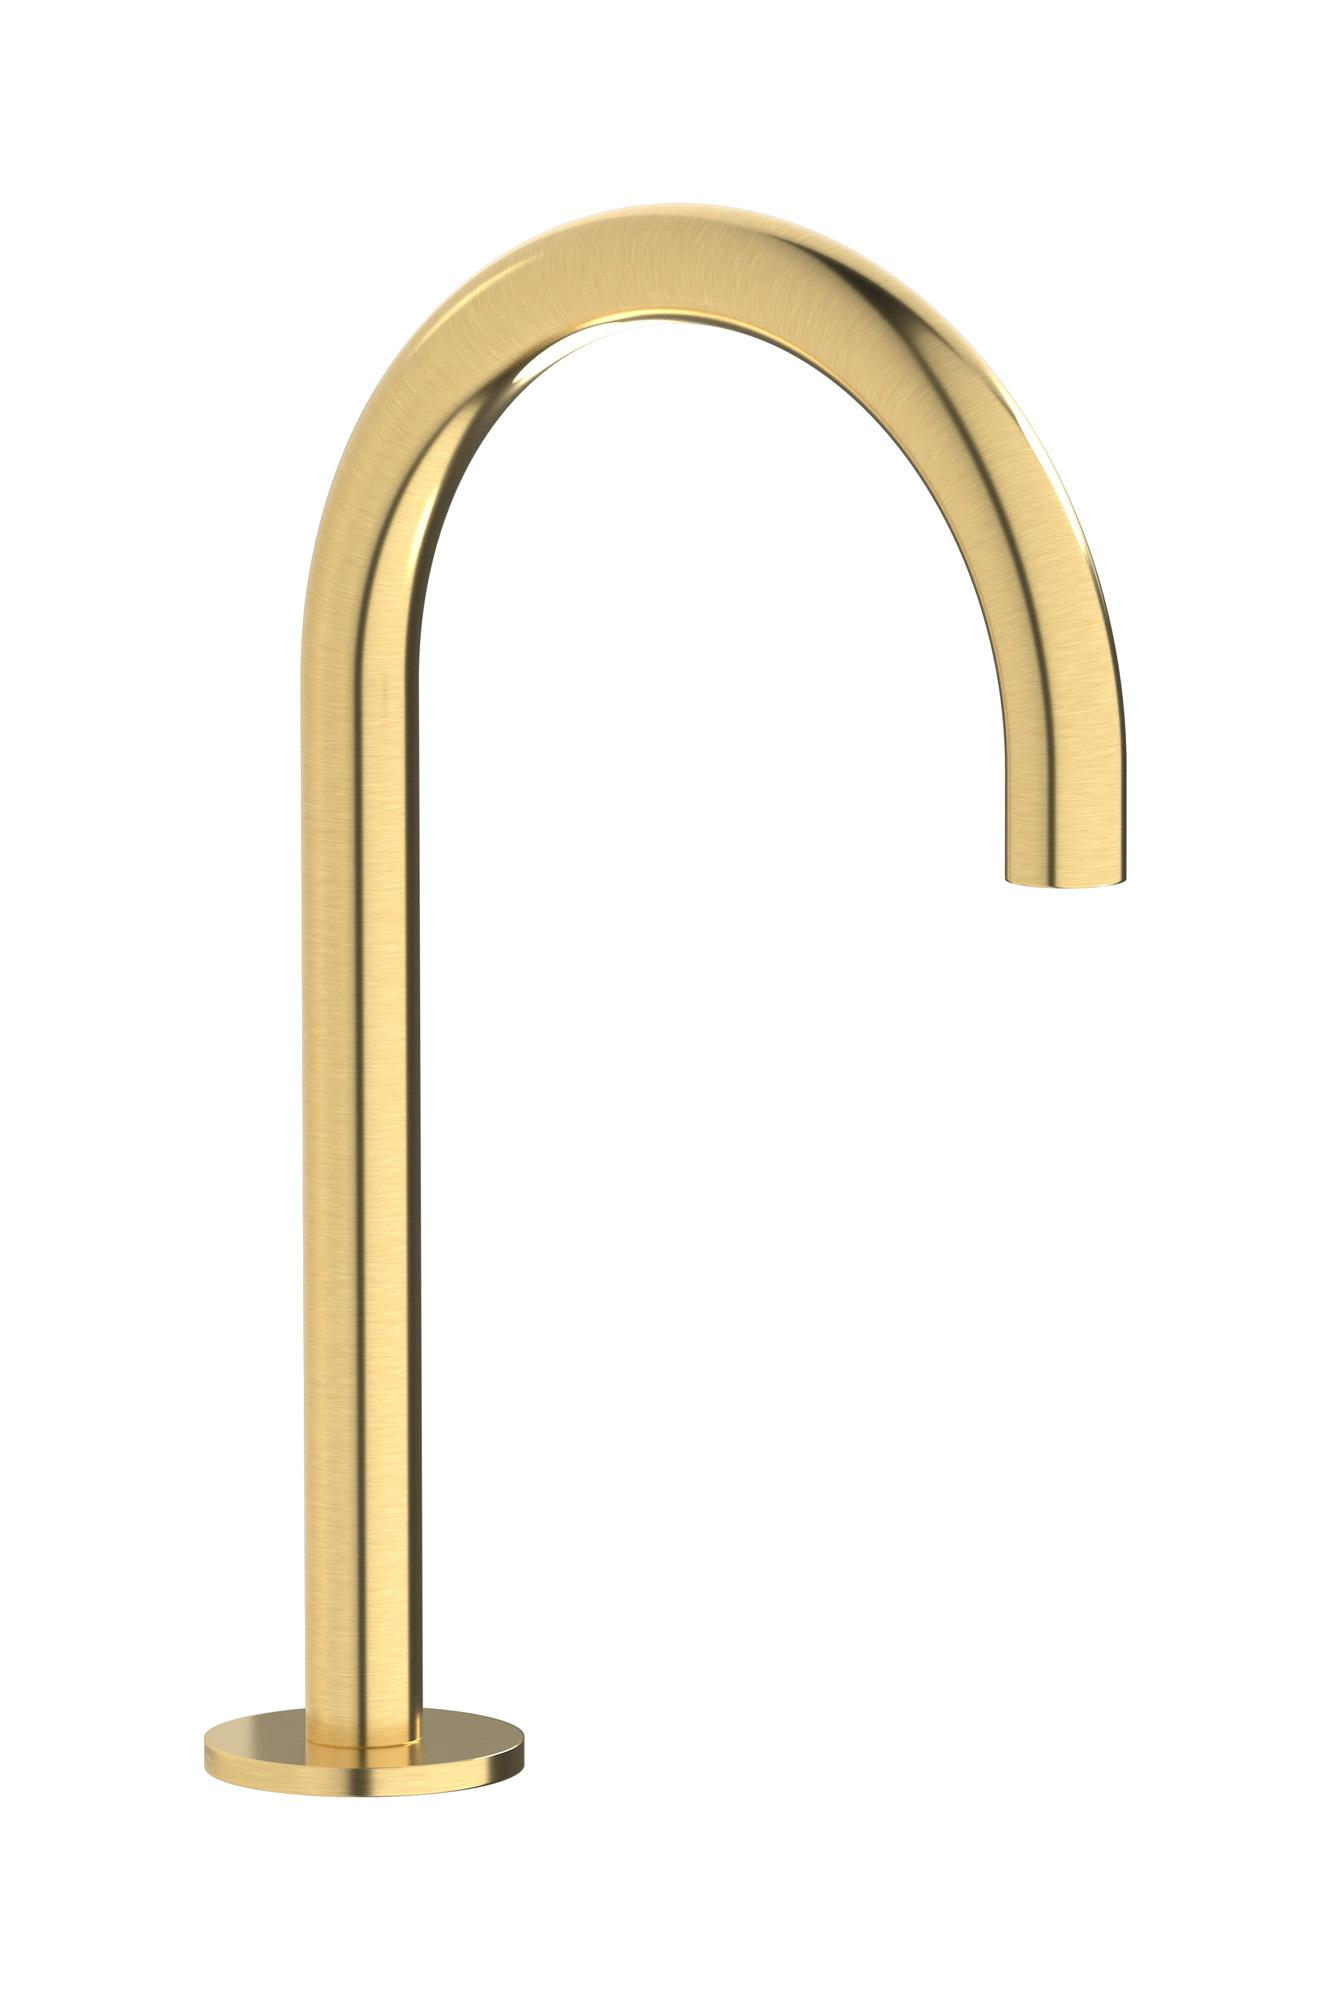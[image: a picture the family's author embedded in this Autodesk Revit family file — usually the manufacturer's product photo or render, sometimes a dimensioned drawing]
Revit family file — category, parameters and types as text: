
# Revit family: RX394
name_source: partatom
category: Apparecchi idraulici
units: mm (PartAtom-declared; Revit-internal decimal feet)

## family parameters
Basato su piano di lavoro = No
Condiviso = No
Mantieni orientamento annotazione = No
Numero OmniClass = 23.45.55.17
Punto di calcolo locali = No
Quota connettore circolare = Usa diametro
Sempre verticale = Sì
Taglio con vuoti quando caricato = No
Tipo di parte = Normale
Titolo OmniClass = Mixing Faucets

## types (12) — shared parameters
Commenti sul tipo = Deck mounted spout complete with drain
Connessione CW = No
Connessione HW = No
Connessione di scarico = No
Connessione di ventilazione = No
Descrizione = Deck mounted spout complete with drain
Produttore = IB Rubinetterie S.p.A.
URL = https://www.weareib.it
Water inlet = 10 mm  [stored 0.0328084 ft]
zero-valued in all types: Prospetto di default

## per-type parameters (varying)
| type | Finishes surface | Immagine tipo | Modello |
| Chrome | IB_Chrome | RX394CC.jpg | RX394CC |
| Black Chrome | IB_Black chrome | RX394CF.jpg | RX394CF |
| Brushed Black Chrome | IB_Brushed black chrome | RX394CS.jpg | RX394CS |
| Pale Gold | IB_Pale gold | RX394II.jpg | RX394II |
| Brushed Pale Gold | IB_brushed pale gold | RX394IS.jpg | RX394IS |
| Matt Black | IB_matt black | RX394NP.jpg | RX394NP |
| Natural Brass | IB_Brass | RX394ON.jpg | RX394ON |
| Gold | IB_gold | RX394OO.jpg | RX394OO |
| Brushed Gold | IB_brushed gold | RX394OS.jpg | RX394OS |
| Rose Gold | IB_Rose gold | RX394RS.jpg | RX394RS |
| Brushed Rose Gold | IB_Brushed rose gold | RX394SR.jpg | RX394SR |
| Brushed Nickel | IB_Brushed nickel | RX394SS.jpg | RX394SS |

note: [stored X ft] marks values corroborated as IEEE doubles in the binary element streams (Revit-internal decimal feet)
